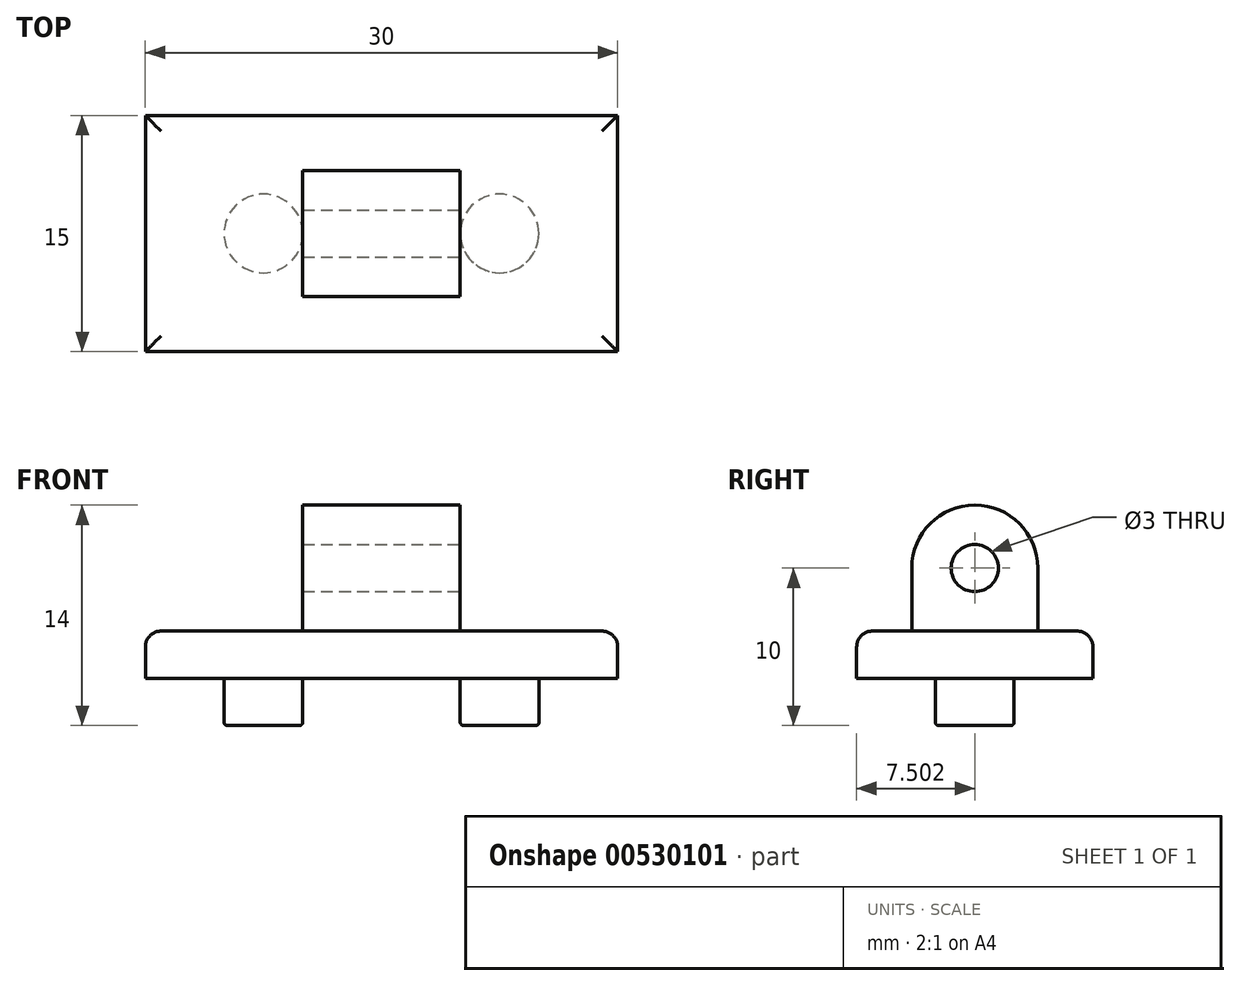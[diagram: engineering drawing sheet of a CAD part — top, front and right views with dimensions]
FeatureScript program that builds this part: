
annotation { "Feature Type Name" : "Feature", "Feature Type Description" : "" }
export const myFeature = defineFeature(function(context is Context, id is Id, definition is map)
    precondition{}
    {
        {
            var Q0;
            Q0=qCreatedBy(makeId("Top.planeOp"),FACE);
            var sketch = newSketch(context, id + "F0", { "sketchPlane" : qUnion([Q0])});
            skLineSegment(sketch, "E0.bottom", {"start": v(-23.5, 10.58) * mm, "end": v(6.5, 10.58) * mm});
            skLineSegment(sketch, "E0.top", {"start": v(-23.5, -4.42) * mm, "end": v(6.5, -4.42) * mm});
            skLineSegment(sketch, "E0.left", {"start": v(-23.5, 10.58) * mm, "end": v(-23.5, -4.42) * mm});
            skLineSegment(sketch, "E0.right", {"start": v(6.5, 10.58) * mm, "end": v(6.5, -4.42) * mm});
            skSolve(sketch);
        }
        {
            var Q0;
            Q0 = qSketchRegion(id + "F0", true);
            extrude(context, id + "F1", {"entities" : qUnion([Q0]), "depth" : 3 * mm, "offsetDistance" : 25 * mm});
        }
        {
            var Q0;
            Q0=makeQuery(id+"F1.opExtrude","CAP_FACE",FACE,{"disambiguationData":[OSD([sQuery(id+"F0.wireOp",EDGE,"E0.bottom"),sQuery(id+"F0.wireOp",EDGE,"E0.top"),sQuery(id+"F0.wireOp",EDGE,"E0.left"),sQuery(id+"F0.wireOp",EDGE,"E0.right")])],"isStart":false});
            var sketch = newSketch(context, id + "F2", { "sketchPlane" : qUnion([Q0])});
            skLineSegment(sketch, "E1.bottom", {"start": v(-13.5, 7.08) * mm, "end": v(-3.5, 7.08) * mm});
            skLineSegment(sketch, "E1.top", {"start": v(-13.5, -0.92) * mm, "end": v(-3.5, -0.92) * mm});
            skLineSegment(sketch, "E1.left", {"start": v(-13.5, 7.08) * mm, "end": v(-13.5, -0.92) * mm});
            skLineSegment(sketch, "E1.right", {"start": v(-3.5, 7.08) * mm, "end": v(-3.5, -0.92) * mm});
            skSolve(sketch);
        }
        {
            var Q0;
            Q0 = qSketchRegion(id + "F2", true);
            extrude(context, id + "F3", {"entities" : qUnion([Q0]), "operationType" : NewBodyOperationType.ADD, "depth" : 8 * mm, "offsetDistance" : 25 * mm});
        }
        {
            var Q0;
            Q0=makeQuery(id+"F3.opExtrude","CAP_EDGE",EDGE,{"disambiguationData":[OSD([sQuery(id+"F2.wireOp",EDGE,"E1.top")])],"isStart":false});
            var Q1;
            Q1=makeQuery(id+"F3.opExtrude","CAP_EDGE",EDGE,{"disambiguationData":[OSD([sQuery(id+"F2.wireOp",EDGE,"E1.bottom")])],"isStart":false});
            fillet(context, id + "F4", {"entities" : qUnion([Q0, Q1]), "radius" : 4 * mm, "tangentPropagation" : true, "allowEdgeOverflow" : false});
        }
        {
            var Q0;
            Q0=makeQuery(id+"F3.opExtrude","SWEPT_FACE",FACE,{"disambiguationData":[OSD([sQuery(id+"F2.wireOp",EDGE,"E1.right")])]});
            var sketch = newSketch(context, id + "F5", { "sketchPlane" : qUnion([Q0])});
            skCircle(sketch, "E2", {"center": v(3.08, 7) * mm, "radius": 1.5 * mm});
            skSolve(sketch);
        }
        {
            var Q0;
            Q0=makeQuery(id+"F5.imprint","IMPRINT",FACE,{"disambiguationData":[TD([[makeQuery(id+"F5.imprint","IMPRINT",EDGE,{"derivedFrom":sQuery(id+"F5.wireOp",EDGE,"E2")}),1.0]])]});
            extrude(context, id + "F6", {"entities" : qUnion([Q0]), "operationType" : NewBodyOperationType.REMOVE, "oppositeDirection" : true, "depth" : 25 * mm, "offsetDistance" : 25 * mm});
        }
        {
            var Q0;
            Q0=makeQuery(id+"F1.opExtrude","CAP_EDGE",EDGE,{"disambiguationData":[OSD([sQuery(id+"F0.wireOp",EDGE,"E0.left")])],"isStart":false});
            var Q1;
            Q1=makeQuery(id+"F1.opExtrude","CAP_EDGE",EDGE,{"disambiguationData":[OSD([sQuery(id+"F0.wireOp",EDGE,"E0.bottom")])],"isStart":false});
            var Q2;
            Q2=makeQuery(id+"F1.opExtrude","CAP_EDGE",EDGE,{"disambiguationData":[OSD([sQuery(id+"F0.wireOp",EDGE,"E0.right")])],"isStart":false});
            var Q3;
            Q3=makeQuery(id+"F1.opExtrude","CAP_EDGE",EDGE,{"disambiguationData":[OSD([sQuery(id+"F0.wireOp",EDGE,"E0.top")])],"isStart":false});
            fillet(context, id + "F7", {"entities" : qUnion([Q0, Q1, Q2, Q3]), "radius" : 1 * mm, "tangentPropagation" : true, "allowEdgeOverflow" : false});
        }
        {
            var Q0;
            Q0=makeQuery(id+"F1.opExtrude","CAP_FACE",FACE,{"disambiguationData":[OSD([sQuery(id+"F0.wireOp",EDGE,"E0.bottom"),sQuery(id+"F0.wireOp",EDGE,"E0.top"),sQuery(id+"F0.wireOp",EDGE,"E0.left"),sQuery(id+"F0.wireOp",EDGE,"E0.right")])],"isStart":true});
            var sketch = newSketch(context, id + "F8", { "sketchPlane" : qUnion([Q0])});
            skCircle(sketch, "E3", {"center": v(-16, -3.08) * mm, "radius": 2.5 * mm});
            skCircle(sketch, "E4", {"center": v(-1, -3.08) * mm, "radius": 2.5 * mm});
            skSolve(sketch);
        }
        {
            var Q0;
            Q0=makeQuery(id+"F8.imprint","IMPRINT",FACE,{"disambiguationData":[TD([[makeQuery(id+"F8.imprint","IMPRINT",EDGE,{"derivedFrom":sQuery(id+"F8.wireOp",EDGE,"E3")}),1.0]])]});
            var Q1;
            Q1=makeQuery(id+"F8.imprint","IMPRINT",FACE,{"disambiguationData":[TD([[makeQuery(id+"F8.imprint","IMPRINT",EDGE,{"derivedFrom":sQuery(id+"F8.wireOp",EDGE,"E4")}),1.0]])]});
            extrude(context, id + "F9", {"entities" : qUnion([Q0, Q1]), "operationType" : NewBodyOperationType.ADD, "depth" : 3 * mm, "offsetDistance" : 25 * mm});
        }
        {
            var Q0;
            Q0=makeQuery(id+"F9.opExtrude","CAP_FACE",FACE,{"disambiguationData":[OSD([sQuery(id+"F8.wireOp",EDGE,"E3")])],"isStart":false});
            var Q1;
            Q1=makeQuery(id+"F9.opExtrude","CAP_FACE",FACE,{"disambiguationData":[OSD([sQuery(id+"F8.wireOp",EDGE,"E4")])],"isStart":false});
            fillet(context, id + "F10", {"entities" : qUnion([Q0, Q1]), "radius" : 0.2 * mm, "tangentPropagation" : true, "allowEdgeOverflow" : false});
        }
    });
